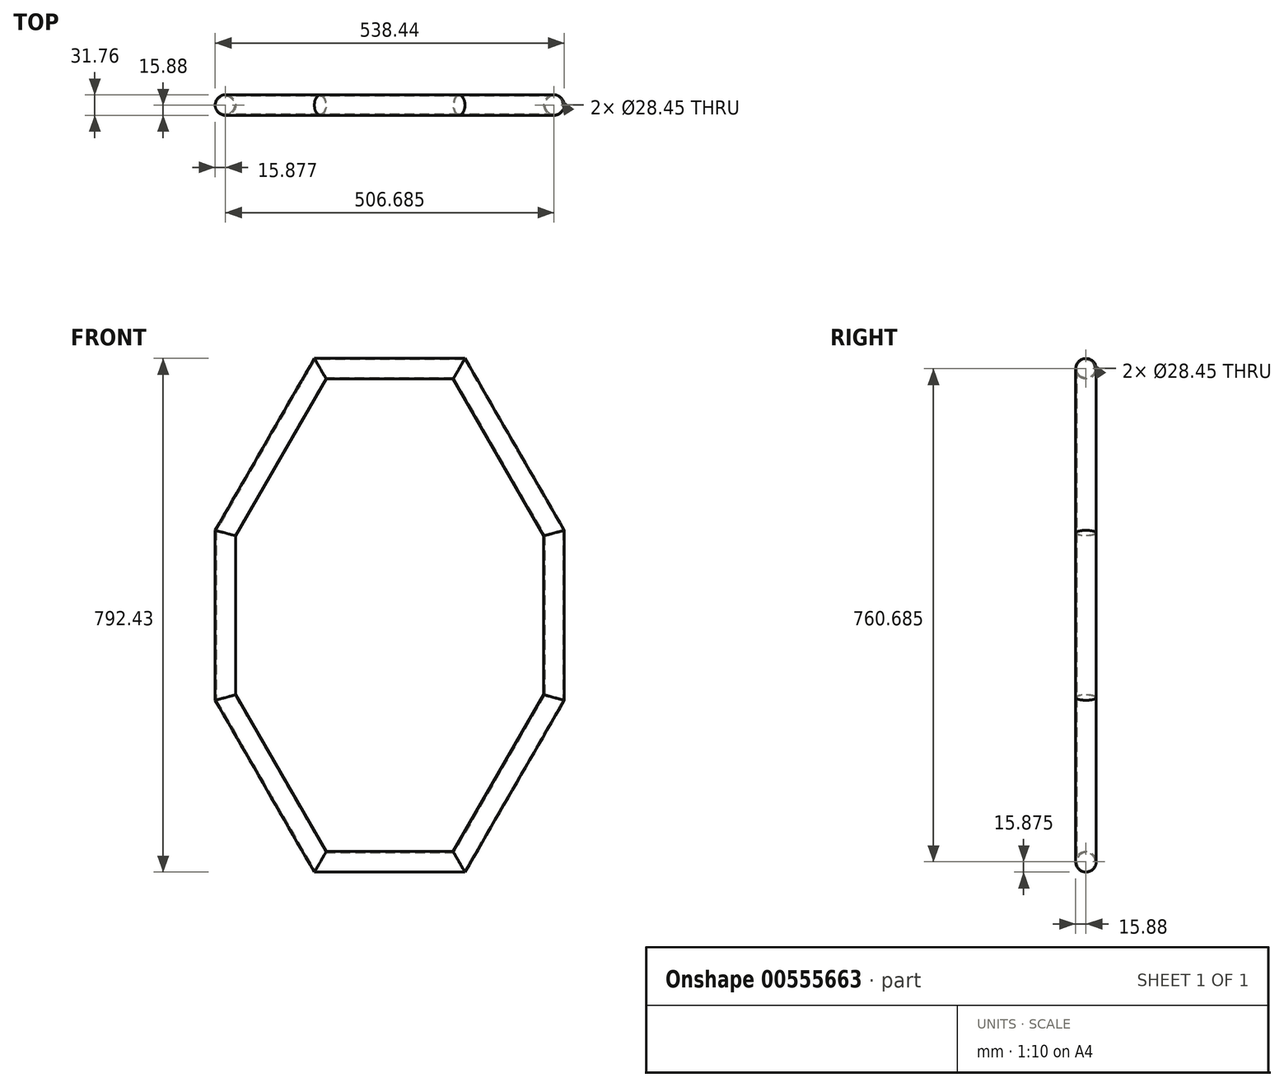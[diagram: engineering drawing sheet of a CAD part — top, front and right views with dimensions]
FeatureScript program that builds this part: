
annotation { "Feature Type Name" : "Feature", "Feature Type Description" : "" }
export const myFeature = defineFeature(function(context is Context, id is Id, definition is map)
    precondition{}
    {
        {
            var Q0;
            Q0=qCreatedBy(makeId("Front.planeOp"),FACE);
            var sketch = newSketch(context, id + "F0", { "sketchPlane" : qUnion([Q0])});
            skLineSegment(sketch, "E0", {"start": v(0, 98.1) * mm, "end": v(-107.35, 98.1) * mm});
            skLineSegment(sketch, "E1", {"start": v(-107.35, 98.1) * mm, "end": v(-254, -155.9) * mm});
            skLineSegment(sketch, "E2", {"start": v(-254, -155.9) * mm, "end": v(-254, -409.9) * mm});
            skLineSegment(sketch, "E3", {"start": v(-254, -409.9) * mm, "end": v(-107.35, -663.9) * mm});
            skLineSegment(sketch, "E4", {"start": v(-107.35, -663.9) * mm, "end": v(0, -663.9) * mm});
            skSolve(sketch);
        }
        {
            var Q0;
            Q0=qCreatedBy(makeId("Right.planeOp"),FACE);
            var sketch = newSketch(context, id + "F1", { "sketchPlane" : qUnion([Q0])});
            skCircle(sketch, "E5", {"center": v(0, 97.45) * mm, "radius": 15.88 * mm});
            skCircle(sketch, "E6", {"center": v(0, 97.45) * mm, "radius": 14.22 * mm});
            skSolve(sketch);
        }
        {
            var Q0;
            Q0=makeQuery(id+"F1.imprint","IMPRINT",FACE,{"disambiguationData":[TD([[makeQuery(id+"F1.imprint","IMPRINT",EDGE,{"derivedFrom":sQuery(id+"F1.wireOp",EDGE,"E5")}),-1.0]])]});
            var Q1;
            Q1=makeQuery(id+"F1.imprint","IMPRINT",FACE,{"disambiguationData":[TD([[makeQuery(id+"F1.imprint","IMPRINT",EDGE,{"derivedFrom":sQuery(id+"F1.wireOp",EDGE,"E5")}),1.0]])]});
            var Q2;
            Q2=sQuery(id+"F0.wireOp",EDGE,"E0");
            var Q3;
            Q3=sQuery(id+"F0.wireOp",EDGE,"E1");
            var Q4;
            Q4=sQuery(id+"F0.wireOp",EDGE,"E2");
            var Q5;
            Q5=sQuery(id+"F0.wireOp",EDGE,"E3");
            var Q6;
            Q6=sQuery(id+"F0.wireOp",EDGE,"E4");
            sweep(context, id + "F2", {"profiles" : qUnion([Q0, Q1]), "path" : qUnion([Q2, Q3, Q4, Q5, Q6])});
        }
        {
            var Q0;
            Q0=makeQuery(id+"F2.opSweep","SWEPT_BODY",BODY,{"disambiguationData":[OSD([sQuery(id+"F0.wireOp",EDGE,"E4"),sQuery(id+"F1.wireOp",EDGE,"E5"),sQuery(id+"F1.wireOp",EDGE,"E6")])]});
            var Q1;
            Q1=qCreatedBy(makeId("Right.planeOp"),FACE);
            mirror(context, id + "F3", {"operationType" : NewBodyOperationType.ADD, "entities" : qUnion([Q0]), "mirrorPlane" : qUnion([Q1])});
        }
    });
